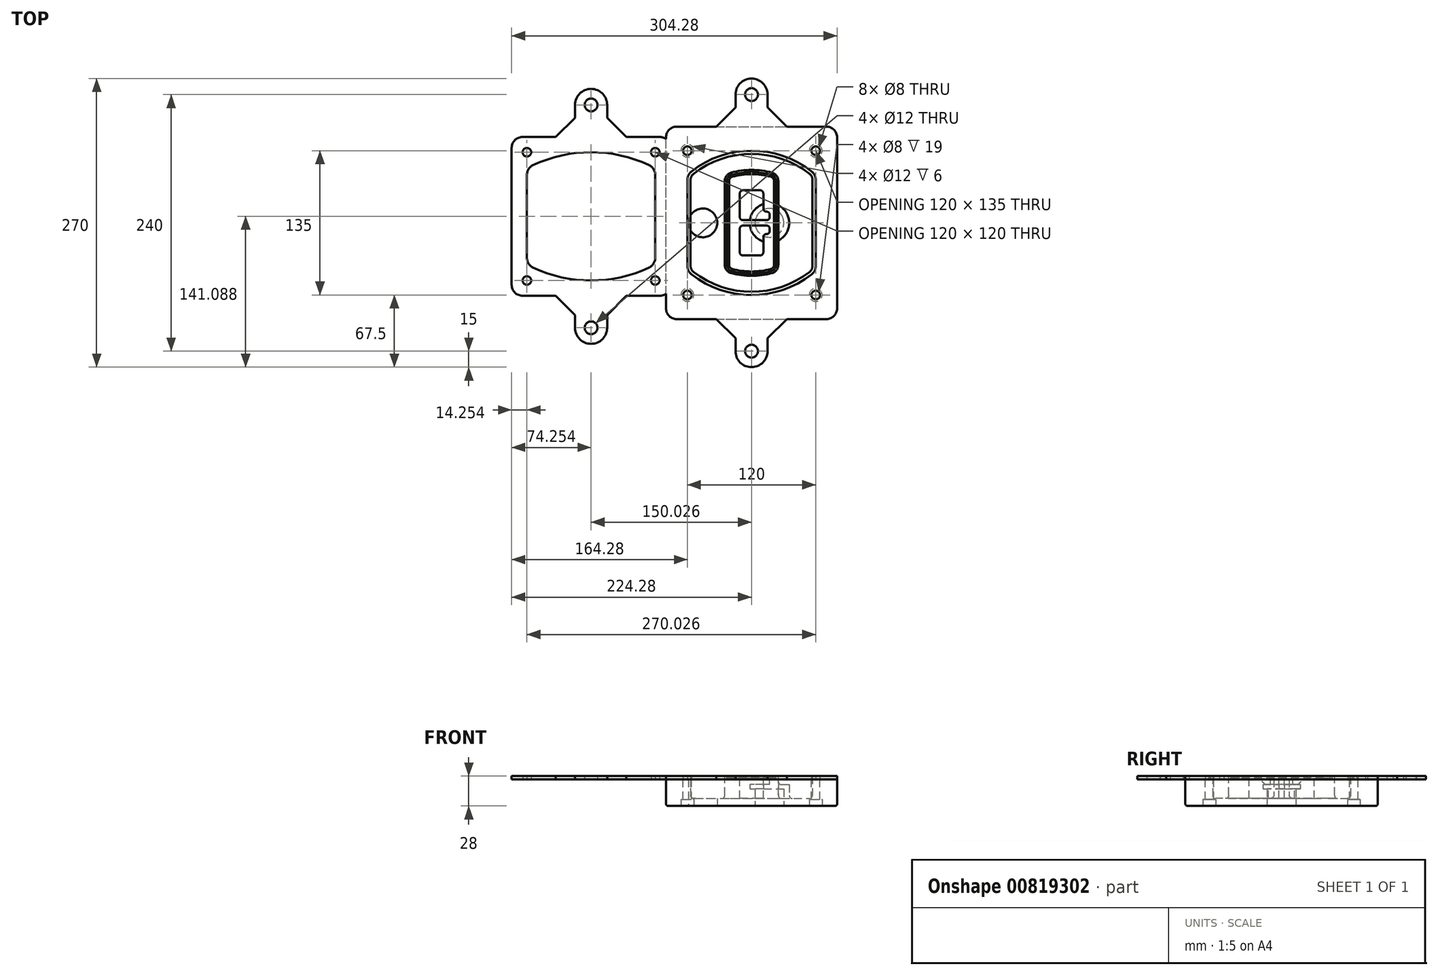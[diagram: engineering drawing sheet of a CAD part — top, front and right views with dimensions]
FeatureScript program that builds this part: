
annotation { "Feature Type Name" : "Feature", "Feature Type Description" : "" }
export const myFeature = defineFeature(function(context is Context, id is Id, definition is map)
    precondition{}
    {
        {
            var Q0;
            Q0=qCreatedBy(makeId("Top.planeOp"),FACE);
            var sketch = newSketch(context, id + "F0", { "sketchPlane" : qUnion([Q0])});
            skPoint(sketch, "E0.rect.middle", {"position": v(0, 0) * mm});
            skLineSegment(sketch, "E1.bottom", {"start": v(-70, -90) * mm, "end": v(70, -90) * mm});
            skLineSegment(sketch, "E1.top", {"start": v(-70, 90) * mm, "end": v(70, 90) * mm});
            skLineSegment(sketch, "E1.left", {"start": v(-80, -80) * mm, "end": v(-80, 80) * mm});
            skLineSegment(sketch, "E1.right", {"start": v(80, -80) * mm, "end": v(80, 80) * mm});
            skLineSegment(sketch, "E2", {"start": v(-80, 90) * mm, "end": v(80, -90) * mm, "construction": true});
            skLineSegment(sketch, "E3", {"start": v(80, 90) * mm, "end": v(-80, -90) * mm, "construction": true});
            skCircle(sketch, "E4", {"center": v(-60, 67.5) * mm, "radius": 4 * mm});
            skCircle(sketch, "E5", {"center": v(60, 67.5) * mm, "radius": 4 * mm});
            skCircle(sketch, "E6", {"center": v(60, -67.5) * mm, "radius": 4 * mm});
            skCircle(sketch, "E7", {"center": v(-60, -67.5) * mm, "radius": 4 * mm});
            skLineSegment(sketch, "E8", {"start": v(-60, 67.5) * mm, "end": v(60, 67.5) * mm, "construction": true});
            skLineSegment(sketch, "E9", {"start": v(60, 67.5) * mm, "end": v(60, -67.5) * mm, "construction": true});
            skLineSegment(sketch, "E10", {"start": v(60, -67.5) * mm, "end": v(-60, -67.5) * mm, "construction": true});
            skLineSegment(sketch, "E11", {"start": v(-60, -67.5) * mm, "end": v(-60, 67.5) * mm, "construction": true});
            skLineSegment(sketch, "E12", {"start": v(-60, 40.3) * mm, "end": v(-60, -40.3) * mm});
            skLineSegment(sketch, "E13", {"start": v(60, 40.3) * mm, "end": v(60, -40.3) * mm});
            skArc(sketch, "E14", {"start": v(56.15, 48.18) * mm, "mid": v(0, 67.5) * mm, "end": v(-56.15, 48.18) * mm});
            skArc(sketch, "E15", {"start": v(-56.15, -48.18) * mm, "mid": v(0, -67.5) * mm, "end": v(56.15, -48.18) * mm});
            skLineSegment(sketch, "E16", {"start": v(-60, 0) * mm, "end": v(60, 0) * mm, "construction": true});
            skPoint(sketch, "E17.visualSharp", {"position": v(-60, -45) * mm});
            skArc(sketch, "E17.filletArc", {"start": v(-60, -40.3) * mm, "mid": v(-58.99, -44.68) * mm, "end": v(-56.15, -48.18) * mm});
            skPoint(sketch, "E18.visualSharp", {"position": v(-60, 45) * mm});
            skArc(sketch, "E18.filletArc", {"start": v(-56.15, 48.18) * mm, "mid": v(-58.99, 44.68) * mm, "end": v(-60, 40.3) * mm});
            skPoint(sketch, "E19.visualSharp", {"position": v(60, 45) * mm});
            skArc(sketch, "E19.filletArc", {"start": v(60, 40.3) * mm, "mid": v(58.99, 44.68) * mm, "end": v(56.15, 48.18) * mm});
            skPoint(sketch, "E20.visualSharp", {"position": v(60, -45) * mm});
            skArc(sketch, "E20.filletArc", {"start": v(56.15, -48.18) * mm, "mid": v(58.99, -44.68) * mm, "end": v(60, -40.3) * mm});
            skPoint(sketch, "E21.visualSharp", {"position": v(-80, 90) * mm});
            skArc(sketch, "E21.filletArc", {"start": v(-70, 90) * mm, "mid": v(-77.07, 87.07) * mm, "end": v(-80, 80) * mm});
            skPoint(sketch, "E22.visualSharp", {"position": v(80, 90) * mm});
            skArc(sketch, "E22.filletArc", {"start": v(80, 80) * mm, "mid": v(77.07, 87.07) * mm, "end": v(70, 90) * mm});
            skPoint(sketch, "E23.visualSharp", {"position": v(80, -90) * mm});
            skArc(sketch, "E23.filletArc", {"start": v(70, -90) * mm, "mid": v(77.07, -87.07) * mm, "end": v(80, -80) * mm});
            skPoint(sketch, "E24.visualSharp", {"position": v(-80, -90) * mm});
            skArc(sketch, "E24.filletArc", {"start": v(-80, -80) * mm, "mid": v(-77.07, -87.07) * mm, "end": v(-70, -90) * mm});
            skArc(sketch, "E25.0", {"start": v(57, 40.3) * mm, "mid": v(56.3, 43.36) * mm, "end": v(54.3, 45.81) * mm});
            skLineSegment(sketch, "E25.1", {"start": v(57, 40.3) * mm, "end": v(57, -40.3) * mm});
            skArc(sketch, "E25.2", {"start": v(54.3, -45.81) * mm, "mid": v(56.3, -43.36) * mm, "end": v(57, -40.3) * mm});
            skArc(sketch, "E25.3", {"start": v(-54.3, -45.81) * mm, "mid": v(0, -64.5) * mm, "end": v(54.3, -45.81) * mm});
            skArc(sketch, "E25.4", {"start": v(-57, -40.3) * mm, "mid": v(-56.3, -43.36) * mm, "end": v(-54.3, -45.81) * mm});
            skArc(sketch, "E25.5", {"start": v(54.3, 45.81) * mm, "mid": v(0, 64.5) * mm, "end": v(-54.3, 45.81) * mm});
            skLineSegment(sketch, "E25.6", {"start": v(-57, 40.3) * mm, "end": v(-57, -40.3) * mm});
            skArc(sketch, "E25.7", {"start": v(-54.3, 45.81) * mm, "mid": v(-56.3, 43.36) * mm, "end": v(-57, 40.3) * mm});
            skArc(sketch, "E26.0", {"start": v(-58.62, 51.33) * mm, "mid": v(-62.58, 46.43) * mm, "end": v(-64, 40.3) * mm});
            skArc(sketch, "E26.1", {"start": v(58.62, 51.33) * mm, "mid": v(0, 71.5) * mm, "end": v(-58.62, 51.33) * mm});
            skArc(sketch, "E26.2", {"start": v(64, 40.3) * mm, "mid": v(62.58, 46.43) * mm, "end": v(58.62, 51.33) * mm});
            skLineSegment(sketch, "E26.3", {"start": v(64, 40.3) * mm, "end": v(64, -40.3) * mm});
            skArc(sketch, "E26.4", {"start": v(58.62, -51.33) * mm, "mid": v(62.58, -46.43) * mm, "end": v(64, -40.3) * mm});
            skLineSegment(sketch, "E26.5", {"start": v(-64, 40.3) * mm, "end": v(-64, -40.3) * mm});
            skArc(sketch, "E26.6", {"start": v(-58.62, -51.33) * mm, "mid": v(0, -71.5) * mm, "end": v(58.62, -51.33) * mm});
            skArc(sketch, "E26.7", {"start": v(-64, -40.3) * mm, "mid": v(-62.58, -46.43) * mm, "end": v(-58.62, -51.33) * mm});
            skSolve(sketch);
        }
        {
            var Q0;
            Q0=makeQuery(id+"F0.imprint","IMPRINT",FACE,{"disambiguationData":[TD([[makeQuery(id+"F0.imprint","IMPRINT",EDGE,{"derivedFrom":sQuery(id+"F0.wireOp",EDGE,"E1.bottom")}),1.0]])]});
            var Q1;
            Q1=makeQuery(id+"F0.imprint","IMPRINT",FACE,{"disambiguationData":[TD([[makeQuery(id+"F0.imprint","IMPRINT",EDGE,{"derivedFrom":sQuery(id+"F0.wireOp",EDGE,"E12")}),1.0]])]});
            var Q2;
            Q2=makeQuery(id+"F0.imprint","IMPRINT",FACE,{"disambiguationData":[TD([[makeQuery(id+"F0.imprint","IMPRINT",EDGE,{"derivedFrom":sQuery(id+"F0.wireOp",EDGE,"E25.0")}),1.0]])]});
            var Q3;
            Q3=makeQuery(id+"F0.imprint","IMPRINT",FACE,{"disambiguationData":[TD([[makeQuery(id+"F0.imprint","IMPRINT",EDGE,{"derivedFrom":sQuery(id+"F0.wireOp",EDGE,"E12")}),-1.0]])]});
            extrude(context, id + "F1", {"entities" : qUnion([Q0, Q1, Q2, Q3]), "oppositeDirection" : true, "depth" : 25 * mm});
        }
        {
            var Q0;
            Q0=makeQuery(id+"F0.imprint","IMPRINT",FACE,{"disambiguationData":[TD([[makeQuery(id+"F0.imprint","IMPRINT",EDGE,{"derivedFrom":sQuery(id+"F0.wireOp",EDGE,"E12")}),1.0]])]});
            extrude(context, id + "F2", {"entities" : qUnion([Q0]), "operationType" : NewBodyOperationType.ADD, "depth" : 3 * mm});
        }
        {
            var Q0;
            Q0=makeQuery(id+"F0.imprint","IMPRINT",FACE,{"disambiguationData":[TD([[makeQuery(id+"F0.imprint","IMPRINT",EDGE,{"derivedFrom":sQuery(id+"F0.wireOp",EDGE,"E25.0")}),1.0]])]});
            extrude(context, id + "F3", {"entities" : qUnion([Q0]), "operationType" : NewBodyOperationType.REMOVE, "oppositeDirection" : true, "depth" : 18 * mm});
        }
        {
            var Q0;
            Q0=makeQuery(id+"F2.opExtrude","CAP_FACE",FACE,{"disambiguationData":[OSD([sQuery(id+"F0.wireOp",EDGE,"E12"),sQuery(id+"F0.wireOp",EDGE,"E13"),sQuery(id+"F0.wireOp",EDGE,"E14"),sQuery(id+"F0.wireOp",EDGE,"E15"),sQuery(id+"F0.wireOp",EDGE,"E17.filletArc"),sQuery(id+"F0.wireOp",EDGE,"E18.filletArc"),sQuery(id+"F0.wireOp",EDGE,"E19.filletArc"),sQuery(id+"F0.wireOp",EDGE,"E20.filletArc"),sQuery(id+"F0.wireOp",EDGE,"E25.0"),sQuery(id+"F0.wireOp",EDGE,"E25.1"),sQuery(id+"F0.wireOp",EDGE,"E25.2"),sQuery(id+"F0.wireOp",EDGE,"E25.3"),sQuery(id+"F0.wireOp",EDGE,"E25.4"),sQuery(id+"F0.wireOp",EDGE,"E25.5"),sQuery(id+"F0.wireOp",EDGE,"E25.6"),sQuery(id+"F0.wireOp",EDGE,"E25.7")])],"isStart":false});
            var sketch = newSketch(context, id + "F4", { "sketchPlane" : qUnion([Q0])});
            skArc(sketch, "E27.0", {"start": v(-19.08, -46.97) * mm, "mid": v(0, -49.5) * mm, "end": v(19.08, -46.97) * mm});
            skArc(sketch, "E28.0", {"start": v(19.08, 46.97) * mm, "mid": v(0, 49.5) * mm, "end": v(-19.08, 46.97) * mm});
            skLineSegment(sketch, "E29", {"start": v(-25, 39.25) * mm, "end": v(-25, -39.25) * mm});
            skLineSegment(sketch, "E30", {"start": v(25, 39.25) * mm, "end": v(25, -39.25) * mm});
            skLineSegment(sketch, "E31", {"start": v(-25, 45.1) * mm, "end": v(25, 45.1) * mm, "construction": true});
            skLineSegment(sketch, "E32", {"start": v(-25, -45.1) * mm, "end": v(25, -45.1) * mm, "construction": true});
            skPoint(sketch, "E33.visualSharp", {"position": v(-25, 45.1) * mm});
            skArc(sketch, "E33.filletArc", {"start": v(-19.08, 46.97) * mm, "mid": v(-23.35, 44.11) * mm, "end": v(-25, 39.25) * mm});
            skPoint(sketch, "E34.visualSharp", {"position": v(25, 45.1) * mm});
            skArc(sketch, "E34.filletArc", {"start": v(25, 39.25) * mm, "mid": v(23.35, 44.11) * mm, "end": v(19.08, 46.97) * mm});
            skPoint(sketch, "E35.visualSharp", {"position": v(25, -45.1) * mm});
            skArc(sketch, "E35.filletArc", {"start": v(19.08, -46.97) * mm, "mid": v(23.35, -44.11) * mm, "end": v(25, -39.25) * mm});
            skPoint(sketch, "E36.visualSharp", {"position": v(-25, -45.1) * mm});
            skArc(sketch, "E36.filletArc", {"start": v(-25, -39.25) * mm, "mid": v(-23.35, -44.11) * mm, "end": v(-19.08, -46.97) * mm});
            skArc(sketch, "E37.0", {"start": v(54.3, 45.81) * mm, "mid": v(0, 64.5) * mm, "end": v(-54.3, 45.81) * mm});
            skArc(sketch, "E37.1", {"start": v(-54.3, 45.81) * mm, "mid": v(-56.3, 43.36) * mm, "end": v(-57, 40.3) * mm});
            skLineSegment(sketch, "E37.2", {"start": v(-57, 40.3) * mm, "end": v(-57, -40.3) * mm});
            skArc(sketch, "E37.3", {"start": v(-57, -40.3) * mm, "mid": v(-56.3, -43.36) * mm, "end": v(-54.3, -45.81) * mm});
            skArc(sketch, "E37.4", {"start": v(-54.3, -45.81) * mm, "mid": v(0, -64.5) * mm, "end": v(54.3, -45.81) * mm});
            skArc(sketch, "E37.5", {"start": v(54.3, -45.81) * mm, "mid": v(56.3, -43.36) * mm, "end": v(57, -40.3) * mm});
            skLineSegment(sketch, "E37.6", {"start": v(57, 40.3) * mm, "end": v(57, -40.3) * mm});
            skArc(sketch, "E37.7", {"start": v(57, 40.3) * mm, "mid": v(56.3, 43.36) * mm, "end": v(54.3, 45.81) * mm});
            skLineSegment(sketch, "E38.0", {"start": v(23, 39.25) * mm, "end": v(23, -39.25) * mm});
            skArc(sketch, "E38.1", {"start": v(18.56, -45.04) * mm, "mid": v(21.76, -42.9) * mm, "end": v(23, -39.25) * mm});
            skArc(sketch, "E38.2", {"start": v(-18.56, -45.04) * mm, "mid": v(0, -47.5) * mm, "end": v(18.56, -45.04) * mm});
            skArc(sketch, "E38.3", {"start": v(-23, -39.25) * mm, "mid": v(-21.76, -42.9) * mm, "end": v(-18.56, -45.04) * mm});
            skLineSegment(sketch, "E38.4", {"start": v(-23, 39.25) * mm, "end": v(-23, -39.25) * mm});
            skArc(sketch, "E38.5", {"start": v(23, 39.25) * mm, "mid": v(21.76, 42.9) * mm, "end": v(18.56, 45.04) * mm});
            skArc(sketch, "E38.6", {"start": v(-18.56, 45.04) * mm, "mid": v(-21.76, 42.9) * mm, "end": v(-23, 39.25) * mm});
            skArc(sketch, "E38.7", {"start": v(18.56, 45.04) * mm, "mid": v(0, 47.5) * mm, "end": v(-18.56, 45.04) * mm});
            skArc(sketch, "E39.0", {"start": v(21, 39.25) * mm, "mid": v(20.18, 41.68) * mm, "end": v(18.04, 43.1) * mm});
            skLineSegment(sketch, "E39.1", {"start": v(21, 39.25) * mm, "end": v(21, -39.25) * mm});
            skArc(sketch, "E39.2", {"start": v(18.04, -43.1) * mm, "mid": v(20.18, -41.68) * mm, "end": v(21, -39.25) * mm});
            skArc(sketch, "E39.3", {"start": v(-18.04, -43.1) * mm, "mid": v(0, -45.5) * mm, "end": v(18.04, -43.1) * mm});
            skArc(sketch, "E39.4", {"start": v(-21, -39.25) * mm, "mid": v(-20.18, -41.68) * mm, "end": v(-18.04, -43.1) * mm});
            skArc(sketch, "E39.5", {"start": v(18.04, 43.1) * mm, "mid": v(0, 45.5) * mm, "end": v(-18.04, 43.1) * mm});
            skLineSegment(sketch, "E39.6", {"start": v(-21, 39.25) * mm, "end": v(-21, -39.25) * mm});
            skArc(sketch, "E39.7", {"start": v(-18.04, 43.1) * mm, "mid": v(-20.18, 41.68) * mm, "end": v(-21, 39.25) * mm});
            skLineSegment(sketch, "E40", {"start": v(-25, 0) * mm, "end": v(25, 0) * mm, "construction": true});
            skLineSegment(sketch, "E41", {"start": v(-11, 5.5) * mm, "end": v(-11, 27.5) * mm});
            skLineSegment(sketch, "E42", {"start": v(-8, 30.5) * mm, "end": v(8, 30.5) * mm});
            skLineSegment(sketch, "E43", {"start": v(11, 27.5) * mm, "end": v(11, 13.5) * mm});
            skLineSegment(sketch, "E44", {"start": v(14, 10.5) * mm, "end": v(14, 10.5) * mm});
            skLineSegment(sketch, "E45", {"start": v(17, 7.5) * mm, "end": v(17, 5.5) * mm});
            skLineSegment(sketch, "E46", {"start": v(14, 2.5) * mm, "end": v(-8, 2.5) * mm});
            skPoint(sketch, "E47.visualSharp", {"position": v(-11, 30.5) * mm});
            skArc(sketch, "E47.filletArc", {"start": v(-8, 30.5) * mm, "mid": v(-10.12, 29.62) * mm, "end": v(-11, 27.5) * mm});
            skPoint(sketch, "E48.visualSharp", {"position": v(11, 30.5) * mm});
            skArc(sketch, "E48.filletArc", {"start": v(11, 27.5) * mm, "mid": v(10.12, 29.62) * mm, "end": v(8, 30.5) * mm});
            skPoint(sketch, "E49.visualSharp", {"position": v(11, 10.5) * mm});
            skArc(sketch, "E49.filletArc", {"start": v(11, 13.5) * mm, "mid": v(11.88, 11.38) * mm, "end": v(14, 10.5) * mm});
            skPoint(sketch, "E50.visualSharp", {"position": v(17, 10.5) * mm});
            skArc(sketch, "E50.filletArc", {"start": v(17, 7.5) * mm, "mid": v(16.12, 9.62) * mm, "end": v(14, 10.5) * mm});
            skPoint(sketch, "E51.visualSharp", {"position": v(17, 2.5) * mm});
            skArc(sketch, "E51.filletArc", {"start": v(14, 2.5) * mm, "mid": v(16.12, 3.38) * mm, "end": v(17, 5.5) * mm});
            skPoint(sketch, "E52.visualSharp", {"position": v(-11, 2.5) * mm});
            skArc(sketch, "E52.filletArc", {"start": v(-11, 5.5) * mm, "mid": v(-10.12, 3.38) * mm, "end": v(-8, 2.5) * mm});
            skLineSegment(sketch, "E53.0.MirrorCS", {"start": v(14, -2.5) * mm, "end": v(-8, -2.5) * mm});
            skArc(sketch, "E54.0.MirrorCS", {"start": v(-11, -5.5) * mm, "mid": v(-10.12, -3.38) * mm, "end": v(-8, -2.5) * mm});
            skLineSegment(sketch, "E55.0.MirrorCS", {"start": v(-11, -5.5) * mm, "end": v(-11, -27.5) * mm});
            skArc(sketch, "E56.0.MirrorCS", {"start": v(-8, -30.5) * mm, "mid": v(-10.12, -29.62) * mm, "end": v(-11, -27.5) * mm});
            skLineSegment(sketch, "E57.0.MirrorCS", {"start": v(-8, -30.5) * mm, "end": v(8, -30.5) * mm});
            skArc(sketch, "E58.0.MirrorCS", {"start": v(11, -27.5) * mm, "mid": v(10.12, -29.62) * mm, "end": v(8, -30.5) * mm});
            skLineSegment(sketch, "E59.0.MirrorCS", {"start": v(11, -27.5) * mm, "end": v(11, -13.5) * mm});
            skArc(sketch, "E60.0.MirrorCS", {"start": v(11, -13.5) * mm, "mid": v(11.88, -11.38) * mm, "end": v(14, -10.5) * mm});
            skArc(sketch, "E61.0.MirrorCS", {"start": v(17, -7.5) * mm, "mid": v(16.12, -9.62) * mm, "end": v(14, -10.5) * mm});
            skLineSegment(sketch, "E62.0.MirrorCS", {"start": v(17, -7.5) * mm, "end": v(17, -5.5) * mm});
            skArc(sketch, "E63.0.MirrorCS", {"start": v(14, -2.5) * mm, "mid": v(16.12, -3.38) * mm, "end": v(17, -5.5) * mm});
            skSolve(sketch);
        }
        {
            var Q0;
            Q0=makeQuery(id+"F4.imprint","IMPRINT",FACE,{"disambiguationData":[TD([[makeQuery(id+"F4.imprint","IMPRINT",EDGE,{"derivedFrom":sQuery(id+"F4.wireOp",EDGE,"E27.0")}),1.0]])]});
            var Q1;
            Q1=makeQuery(id+"F4.imprint","IMPRINT",FACE,{"disambiguationData":[TD([[makeQuery(id+"F4.imprint","IMPRINT",EDGE,{"derivedFrom":sQuery(id+"F4.wireOp",EDGE,"E38.0")}),-1.0]])]});
            var Q2;
            Q2=makeQuery(id+"F4.imprint","IMPRINT",FACE,{"disambiguationData":[TD([[makeQuery(id+"F4.imprint","IMPRINT",EDGE,{"derivedFrom":sQuery(id+"F4.wireOp",EDGE,"E39.0")}),1.0]])]});
            extrude(context, id + "F5", {"entities" : qUnion([Q0, Q1, Q2]), "operationType" : NewBodyOperationType.ADD, "endBound" : BoundingType.UP_TO_NEXT, "oppositeDirection" : true, "depth" : 25 * mm});
        }
        {
            var Q0;
            Q0=makeQuery(id+"F4.imprint","IMPRINT",FACE,{"disambiguationData":[TD([[makeQuery(id+"F4.imprint","IMPRINT",EDGE,{"derivedFrom":sQuery(id+"F4.wireOp",EDGE,"E38.0")}),-1.0]])]});
            extrude(context, id + "F6", {"entities" : qUnion([Q0]), "operationType" : NewBodyOperationType.REMOVE, "oppositeDirection" : true, "depth" : 2 * mm});
        }
        {
            var Q0;
            Q0=makeQuery(id+"F1.opExtrude","CAP_FACE",FACE,{"disambiguationData":[OSD([sQuery(id+"F0.wireOp",EDGE,"E1.bottom"),sQuery(id+"F0.wireOp",EDGE,"E1.top"),sQuery(id+"F0.wireOp",EDGE,"E1.left"),sQuery(id+"F0.wireOp",EDGE,"E1.right"),sQuery(id+"F0.wireOp",EDGE,"E4"),sQuery(id+"F0.wireOp",EDGE,"E5"),sQuery(id+"F0.wireOp",EDGE,"E6"),sQuery(id+"F0.wireOp",EDGE,"E7"),sQuery(id+"F0.wireOp",EDGE,"E21.filletArc"),sQuery(id+"F0.wireOp",EDGE,"E22.filletArc"),sQuery(id+"F0.wireOp",EDGE,"E23.filletArc"),sQuery(id+"F0.wireOp",EDGE,"E24.filletArc")])],"isStart":false});
            var sketch = newSketch(context, id + "F7", { "sketchPlane" : qUnion([Q0])});
            skCircle(sketch, "E64", {"center": v(16.76, 0) * mm, "radius": 13.47 * mm});
            skCircle(sketch, "E65", {"center": v(-45.56, 0) * mm, "radius": 13.47 * mm});
            skLineSegment(sketch, "E66", {"start": v(80, 0) * mm, "end": v(-80, 0) * mm});
            skCircle(sketch, "E67", {"center": v(16.76, 0) * mm, "radius": 18.47 * mm});
            skCircle(sketch, "E68", {"center": v(60, -67.5) * mm, "radius": 6 * mm});
            skCircle(sketch, "E69", {"center": v(-60, -67.5) * mm, "radius": 6 * mm});
            skCircle(sketch, "E70", {"center": v(-60, 67.5) * mm, "radius": 6 * mm});
            skCircle(sketch, "E71", {"center": v(60, 67.5) * mm, "radius": 6 * mm});
            skSolve(sketch);
        }
        {
            var Q0;
            {var subQ1=sQuery(id+"F7.wireOp",EDGE,"E66");var subQ4=sQuery(id+"F7.wireOp",EDGE,"E64");var subQ6=makeQuery(id+"F7.imprint","INTERSECT",VERTEX,{"disambiguationData":[OD(0.0)],"derivedFrom":[subQ4,subQ1]});Q0=makeQuery(id+"F7.imprint","IMPRINT",FACE,{"disambiguationData":[TD([[makeQuery(id+"F7.imprint","IMPRINT",EDGE,{"disambiguationData":[TD([[subQ6,-1.0]])],"derivedFrom":subQ4}),-1.0]])]});}
            var Q1;
            {var subQ0=sQuery(id+"F7.wireOp",EDGE,"E66");var subQ1=sQuery(id+"F7.wireOp",EDGE,"E64");var subQ3=makeQuery(id+"F7.imprint","INTERSECT",VERTEX,{"disambiguationData":[OD(0.0)],"derivedFrom":[subQ1,subQ0]});Q1=makeQuery(id+"F7.imprint","IMPRINT",FACE,{"disambiguationData":[TD([[makeQuery(id+"F7.imprint","IMPRINT",EDGE,{"disambiguationData":[TD([[subQ3,-1.0]])],"derivedFrom":subQ1}),1.0]])]});}
            var Q2;
            {var subQ0=sQuery(id+"F7.wireOp",EDGE,"E66");var subQ1=sQuery(id+"F7.wireOp",EDGE,"E64");var subQ3=makeQuery(id+"F7.imprint","INTERSECT",VERTEX,{"disambiguationData":[OD(0.0)],"derivedFrom":[subQ1,subQ0]});Q2=makeQuery(id+"F7.imprint","IMPRINT",FACE,{"disambiguationData":[TD([[makeQuery(id+"F7.imprint","IMPRINT",EDGE,{"disambiguationData":[TD([[subQ3,1.0]])],"derivedFrom":subQ1}),1.0]])]});}
            var Q3;
            {var subQ1=sQuery(id+"F7.wireOp",EDGE,"E66");var subQ4=sQuery(id+"F7.wireOp",EDGE,"E64");var subQ6=makeQuery(id+"F7.imprint","INTERSECT",VERTEX,{"disambiguationData":[OD(0.0)],"derivedFrom":[subQ4,subQ1]});Q3=makeQuery(id+"F7.imprint","IMPRINT",FACE,{"disambiguationData":[TD([[makeQuery(id+"F7.imprint","IMPRINT",EDGE,{"disambiguationData":[TD([[subQ6,1.0]])],"derivedFrom":subQ4}),-1.0]])]});}
            extrude(context, id + "F8", {"entities" : qUnion([Q0, Q1, Q2, Q3]), "operationType" : NewBodyOperationType.ADD, "oppositeDirection" : true, "depth" : 20 * mm});
        }
        {
            var Q0;
            {var subQ0=sQuery(id+"F7.wireOp",EDGE,"E66");var subQ1=sQuery(id+"F7.wireOp",EDGE,"E64");var subQ3=makeQuery(id+"F7.imprint","INTERSECT",VERTEX,{"disambiguationData":[OD(0.0)],"derivedFrom":[subQ1,subQ0]});Q0=makeQuery(id+"F7.imprint","IMPRINT",FACE,{"disambiguationData":[TD([[makeQuery(id+"F7.imprint","IMPRINT",EDGE,{"disambiguationData":[TD([[subQ3,-1.0]])],"derivedFrom":subQ1}),1.0]])]});}
            var Q1;
            {var subQ0=sQuery(id+"F7.wireOp",EDGE,"E66");var subQ1=sQuery(id+"F7.wireOp",EDGE,"E64");var subQ3=makeQuery(id+"F7.imprint","INTERSECT",VERTEX,{"disambiguationData":[OD(0.0)],"derivedFrom":[subQ1,subQ0]});Q1=makeQuery(id+"F7.imprint","IMPRINT",FACE,{"disambiguationData":[TD([[makeQuery(id+"F7.imprint","IMPRINT",EDGE,{"disambiguationData":[TD([[subQ3,1.0]])],"derivedFrom":subQ1}),1.0]])]});}
            extrude(context, id + "F9", {"entities" : qUnion([Q0, Q1]), "operationType" : NewBodyOperationType.REMOVE, "oppositeDirection" : true, "depth" : 16 * mm});
        }
        {
            var Q0;
            {var subQ0=sQuery(id+"F7.wireOp",EDGE,"E66");var subQ1=sQuery(id+"F7.wireOp",EDGE,"E65");var subQ3=makeQuery(id+"F7.imprint","INTERSECT",VERTEX,{"disambiguationData":[OD(0.0)],"derivedFrom":[subQ1,subQ0]});Q0=makeQuery(id+"F7.imprint","IMPRINT",FACE,{"disambiguationData":[TD([[makeQuery(id+"F7.imprint","IMPRINT",EDGE,{"disambiguationData":[TD([[subQ3,-1.0]])],"derivedFrom":subQ1}),1.0]])]});}
            var Q1;
            {var subQ0=sQuery(id+"F7.wireOp",EDGE,"E66");var subQ1=sQuery(id+"F7.wireOp",EDGE,"E65");var subQ3=makeQuery(id+"F7.imprint","INTERSECT",VERTEX,{"disambiguationData":[OD(0.0)],"derivedFrom":[subQ1,subQ0]});Q1=makeQuery(id+"F7.imprint","IMPRINT",FACE,{"disambiguationData":[TD([[makeQuery(id+"F7.imprint","IMPRINT",EDGE,{"disambiguationData":[TD([[subQ3,1.0]])],"derivedFrom":subQ1}),1.0]])]});}
            extrude(context, id + "F10", {"entities" : qUnion([Q0, Q1]), "operationType" : NewBodyOperationType.REMOVE, "oppositeDirection" : true, "depth" : 25 * mm});
        }
        {
            var Q0;
            Q0=makeQuery(id+"F7.imprint","IMPRINT",FACE,{"disambiguationData":[TD([[makeQuery(id+"F7.imprint","IMPRINT",EDGE,{"derivedFrom":sQuery(id+"F7.wireOp",EDGE,"E68")}),1.0]])]});
            var Q1;
            Q1=makeQuery(id+"F7.imprint","IMPRINT",FACE,{"disambiguationData":[TD([[makeQuery(id+"F7.imprint","IMPRINT",EDGE,{"derivedFrom":makeQuery(id+"F1.opExtrude","CAP_EDGE",EDGE,{"disambiguationData":[OSD([sQuery(id+"F0.wireOp",EDGE,"E5")])],"isStart":false})}),-1.0]])]});
            var Q2;
            Q2=makeQuery(id+"F7.imprint","IMPRINT",FACE,{"disambiguationData":[TD([[makeQuery(id+"F7.imprint","IMPRINT",EDGE,{"derivedFrom":sQuery(id+"F7.wireOp",EDGE,"E69")}),1.0]])]});
            var Q3;
            Q3=makeQuery(id+"F7.imprint","IMPRINT",FACE,{"disambiguationData":[TD([[makeQuery(id+"F7.imprint","IMPRINT",EDGE,{"derivedFrom":makeQuery(id+"F1.opExtrude","CAP_EDGE",EDGE,{"disambiguationData":[OSD([sQuery(id+"F0.wireOp",EDGE,"E4")])],"isStart":false})}),-1.0]])]});
            var Q4;
            Q4=makeQuery(id+"F7.imprint","IMPRINT",FACE,{"disambiguationData":[TD([[makeQuery(id+"F7.imprint","IMPRINT",EDGE,{"derivedFrom":sQuery(id+"F7.wireOp",EDGE,"E70")}),1.0]])]});
            var Q5;
            Q5=makeQuery(id+"F7.imprint","IMPRINT",FACE,{"disambiguationData":[TD([[makeQuery(id+"F7.imprint","IMPRINT",EDGE,{"derivedFrom":makeQuery(id+"F1.opExtrude","CAP_EDGE",EDGE,{"disambiguationData":[OSD([sQuery(id+"F0.wireOp",EDGE,"E7")])],"isStart":false})}),-1.0]])]});
            var Q6;
            Q6=makeQuery(id+"F7.imprint","IMPRINT",FACE,{"disambiguationData":[TD([[makeQuery(id+"F7.imprint","IMPRINT",EDGE,{"derivedFrom":sQuery(id+"F7.wireOp",EDGE,"E71")}),1.0]])]});
            var Q7;
            Q7=makeQuery(id+"F7.imprint","IMPRINT",FACE,{"disambiguationData":[TD([[makeQuery(id+"F7.imprint","IMPRINT",EDGE,{"derivedFrom":makeQuery(id+"F1.opExtrude","CAP_EDGE",EDGE,{"disambiguationData":[OSD([sQuery(id+"F0.wireOp",EDGE,"E6")])],"isStart":false})}),-1.0]])]});
            extrude(context, id + "F11", {"entities" : qUnion([Q0, Q1, Q2, Q3, Q4, Q5, Q6, Q7]), "operationType" : NewBodyOperationType.REMOVE, "oppositeDirection" : true, "depth" : 6 * mm});
        }
        {
            var Q0;
            Q0=makeQuery(id+"F9.boolean.opBoolean","COPY",FACE,{"derivedFrom":makeQuery(id+"F9.opExtrude","CAP_FACE",FACE,{"disambiguationData":[OSD([sQuery(id+"F7.wireOp",EDGE,"E64")])],"isStart":false})});
            var sketch = newSketch(context, id + "F12", { "sketchPlane" : qUnion([Q0])});
            skArc(sketch, "E72.0", {"start": v(11, 17.55) * mm, "mid": v(2.57, 11.82) * mm, "end": v(-1.54, 2.5) * mm});
            skArc(sketch, "E72.1", {"start": v(-1.54, -2.5) * mm, "mid": v(2.57, -11.82) * mm, "end": v(11, -17.55) * mm});
            skLineSegment(sketch, "E73", {"start": v(-1.54, -2.5) * mm, "end": v(14, -2.5) * mm});
            skLineSegment(sketch, "E74.0", {"start": v(14, 2.5) * mm, "end": v(-1.54, 2.5) * mm});
            skArc(sketch, "E74.1", {"start": v(14, 2.5) * mm, "mid": v(16.12, 3.38) * mm, "end": v(17, 5.5) * mm});
            skLineSegment(sketch, "E74.2", {"start": v(17, 7.5) * mm, "end": v(17, 5.5) * mm});
            skArc(sketch, "E74.3", {"start": v(17, 7.5) * mm, "mid": v(16.12, 9.62) * mm, "end": v(14, 10.5) * mm});
            skArc(sketch, "E74.4", {"start": v(11, 13.5) * mm, "mid": v(11.88, 11.38) * mm, "end": v(14, 10.5) * mm});
            skLineSegment(sketch, "E74.5", {"start": v(11, 17.55) * mm, "end": v(11, 13.5) * mm});
            skLineSegment(sketch, "E74.7", {"start": v(14, -2.5) * mm, "end": v(-1.54, -2.5) * mm});
            skArc(sketch, "E74.8", {"start": v(14, -2.5) * mm, "mid": v(16.12, -3.38) * mm, "end": v(17, -5.5) * mm});
            skLineSegment(sketch, "E74.9", {"start": v(17, -7.5) * mm, "end": v(17, -5.5) * mm});
            skArc(sketch, "E74.10", {"start": v(17, -7.5) * mm, "mid": v(16.12, -9.62) * mm, "end": v(14, -10.5) * mm});
            skArc(sketch, "E74.11", {"start": v(11, -13.5) * mm, "mid": v(11.88, -11.38) * mm, "end": v(14, -10.5) * mm});
            skLineSegment(sketch, "E74.12", {"start": v(11, -17.55) * mm, "end": v(11, -13.5) * mm});
            skPoint(sketch, "E75.orphan", {"position": v(11, -27.5) * mm});
            skPoint(sketch, "E76.orphan", {"position": v(-8, -2.5) * mm});
            skPoint(sketch, "E77.orphan", {"position": v(-8, 2.5) * mm});
            skPoint(sketch, "E78.orphan", {"position": v(11, 27.5) * mm});
            skSolve(sketch);
        }
        {
            var Q0;
            {var subQ7=sQuery(id+"F12.wireOp",EDGE,"E72.0");var subQ14=sQuery(id+"F12.wireOp",EDGE,"E72.1");var subQ16=sQuery(id+"F12.wireOp",EDGE,"E74.1");var subQ18=sQuery(id+"F12.wireOp",EDGE,"E74.8");Q0=qUnion([makeQuery(id+"F12.imprint","IMPRINT",FACE,{"disambiguationData":[TD([[makeQuery(id+"F12.imprint","IMPRINT",EDGE,{"derivedFrom":subQ7}),1.0]])]}),makeQuery(id+"F12.imprint","IMPRINT",FACE,{"disambiguationData":[TD([[makeQuery(id+"F12.imprint","IMPRINT",EDGE,{"derivedFrom":subQ14}),1.0]])]}),makeQuery(id+"F12.imprint","IMPRINT",FACE,{"disambiguationData":[TD([[makeQuery(id+"F12.imprint","IMPRINT",EDGE,{"derivedFrom":subQ16}),1.0]])]}),makeQuery(id+"F12.imprint","IMPRINT",FACE,{"disambiguationData":[TD([[makeQuery(id+"F12.imprint","IMPRINT",EDGE,{"derivedFrom":subQ18}),-1.0]])]})]);}
            var Q1;
            Q1=makeQuery(id+"F5.boolean.opBoolean","SPLIT",FACE,{"disambiguationData":[TD([makeQuery(id+"F5.opExtrude","SWEPT_FACE",FACE,{"disambiguationData":[OSD([sQuery(id+"F4.wireOp",EDGE,"E41")])]})])],"derivedFrom":makeQuery(id+"F3.boolean.opBoolean","COPY",FACE,{"derivedFrom":makeQuery(id+"F3.opExtrude","CAP_FACE",FACE,{"disambiguationData":[OSD([sQuery(id+"F0.wireOp",EDGE,"E25.0"),sQuery(id+"F0.wireOp",EDGE,"E25.1"),sQuery(id+"F0.wireOp",EDGE,"E25.2"),sQuery(id+"F0.wireOp",EDGE,"E25.3"),sQuery(id+"F0.wireOp",EDGE,"E25.4"),sQuery(id+"F0.wireOp",EDGE,"E25.5"),sQuery(id+"F0.wireOp",EDGE,"E25.6"),sQuery(id+"F0.wireOp",EDGE,"E25.7")])],"isStart":false})})});
            extrude(context, id + "F13", {"entities" : qUnion([Q0]), "operationType" : NewBodyOperationType.REMOVE, "endBound" : BoundingType.UP_TO_SURFACE, "endBoundEntityFace" : qUnion([Q1]), "depth" : 25 * mm});
        }
        {
            var Q0;
            Q0=makeQuery(id+"F3.boolean.opBoolean","COPY",EDGE,{"derivedFrom":makeQuery(id+"F3.opExtrude","CAP_EDGE",EDGE,{"disambiguationData":[OSD([sQuery(id+"F0.wireOp",EDGE,"E25.6")])],"isStart":false})});
            var Q1;
            Q1=makeQuery(id+"F8.boolean.opBoolean","INTERSECT",EDGE,{"derivedFrom":[makeQuery(id+"F5.opExtrude","SWEPT_FACE",FACE,{"disambiguationData":[OSD([sQuery(id+"F4.wireOp",EDGE,"E30")])]}),makeQuery(id+"F8.opExtrude","CAP_FACE",FACE,{"disambiguationData":[OSD([sQuery(id+"F7.wireOp",EDGE,"E67")])],"isStart":false})]});
            var Q2;
            Q2=makeQuery(id+"F8.boolean.opBoolean","INTERSECT",EDGE,{"disambiguationData":[OD(1.0)],"derivedFrom":[makeQuery(id+"F5.opExtrude","SWEPT_FACE",FACE,{"disambiguationData":[OSD([sQuery(id+"F4.wireOp",EDGE,"E30")])]}),makeQuery(id+"F8.opExtrude","SWEPT_FACE",FACE,{"disambiguationData":[OSD([sQuery(id+"F7.wireOp",EDGE,"E67")])]})]});
            var Q3;
            {var subQ0=sQuery(id+"F4.wireOp",EDGE,"E30");Q3=makeQuery(id+"F8.boolean.opBoolean","SPLIT",EDGE,{"disambiguationData":[TD([makeQuery(id+"F5.opExtrude","SWEPT_FACE",FACE,{"disambiguationData":[OSD([sQuery(id+"F4.wireOp",EDGE,"E35.filletArc")])]})])],"derivedFrom":makeQuery(id+"F5.opExtrude","CAP_EDGE",EDGE,{"disambiguationData":[OSD([subQ0])],"isStart":false})});}
            var Q4;
            {var subQ0=sQuery(id+"F0.wireOp",EDGE,"E25.7");var subQ1=sQuery(id+"F0.wireOp",EDGE,"E25.1");var subQ2=sQuery(id+"F0.wireOp",EDGE,"E25.6");var subQ3=sQuery(id+"F0.wireOp",EDGE,"E25.5");var subQ4=sQuery(id+"F0.wireOp",EDGE,"E25.4");var subQ5=sQuery(id+"F0.wireOp",EDGE,"E25.0");var subQ6=sQuery(id+"F0.wireOp",EDGE,"E25.2");var subQ7=sQuery(id+"F0.wireOp",EDGE,"E25.3");Q4=makeQuery(id+"F8.boolean.opBoolean","INTERSECT",EDGE,{"derivedFrom":[makeQuery(id+"F5.boolean.opBoolean","SPLIT",FACE,{"disambiguationData":[TD([makeQuery(id+"F2.opExtrude","SWEPT_FACE",FACE,{"disambiguationData":[OSD([subQ5])]})])],"derivedFrom":makeQuery(id+"F3.boolean.opBoolean","COPY",FACE,{"derivedFrom":makeQuery(id+"F3.opExtrude","CAP_FACE",FACE,{"disambiguationData":[OSD([subQ5,subQ1,subQ6,subQ7,subQ4,subQ3,subQ2,subQ0])],"isStart":false})})}),makeQuery(id+"F8.opExtrude","SWEPT_FACE",FACE,{"disambiguationData":[OSD([sQuery(id+"F7.wireOp",EDGE,"E67")])]})]});}
            var Q5;
            Q5=makeQuery(id+"F8.boolean.opBoolean","INTERSECT",EDGE,{"disambiguationData":[OD(0.0)],"derivedFrom":[makeQuery(id+"F5.opExtrude","SWEPT_FACE",FACE,{"disambiguationData":[OSD([sQuery(id+"F4.wireOp",EDGE,"E30")])]}),makeQuery(id+"F8.opExtrude","SWEPT_FACE",FACE,{"disambiguationData":[OSD([sQuery(id+"F7.wireOp",EDGE,"E67")])]})]});
            fillet(context, id + "F14", {"entities" : qUnion([Q0, Q1, Q2, Q3, Q4, Q5]), "radius" : 3 * mm, "tangentPropagation" : true, "allowEdgeOverflow" : false});
        }
        {
            var Q0;
            Q0=makeQuery(id+"F1.opExtrude","CAP_EDGE",EDGE,{"disambiguationData":[OSD([sQuery(id+"F0.wireOp",EDGE,"E1.bottom")])],"isStart":false});
            fillet(context, id + "F15", {"entities" : qUnion([Q0]), "radius" : 2 * mm, "tangentPropagation" : true, "allowEdgeOverflow" : false});
        }
        {
            var Q0;
            {var subQ0=sQuery(id+"F0.wireOp",EDGE,"E21.filletArc");var subQ1=sQuery(id+"F0.wireOp",EDGE,"E7");var subQ2=sQuery(id+"F0.wireOp",EDGE,"E6");var subQ3=sQuery(id+"F0.wireOp",EDGE,"E5");var subQ4=sQuery(id+"F0.wireOp",EDGE,"E4");var subQ5=sQuery(id+"F0.wireOp",EDGE,"E22.filletArc");var subQ6=sQuery(id+"F0.wireOp",EDGE,"E1.bottom");var subQ7=sQuery(id+"F0.wireOp",EDGE,"E1.right");var subQ8=sQuery(id+"F0.wireOp",EDGE,"E1.top");var subQ9=sQuery(id+"F0.wireOp",EDGE,"E1.left");var subQ10=sQuery(id+"F0.wireOp",EDGE,"E23.filletArc");var subQ11=sQuery(id+"F0.wireOp",EDGE,"E24.filletArc");Q0=makeQuery(id+"F2.boolean.opBoolean","SPLIT",FACE,{"disambiguationData":[TD([makeQuery(id+"F1.opExtrude","SWEPT_FACE",FACE,{"disambiguationData":[OSD([subQ6])]})])],"derivedFrom":makeQuery(id+"F1.opExtrude","CAP_FACE",FACE,{"disambiguationData":[OSD([subQ6,subQ8,subQ9,subQ7,subQ4,subQ3,subQ2,subQ1,subQ0,subQ5,subQ10,subQ11])],"isStart":true})});}
            var sketch = newSketch(context, id + "F16", { "sketchPlane" : qUnion([Q0])});
            skCircle(sketch, "E79.0", {"center": v(60, 67.5) * mm, "radius": 4 * mm});
            skLineSegment(sketch, "E79.1", {"start": v(80, -80) * mm, "end": v(80, 80) * mm});
            skArc(sketch, "E79.2", {"start": v(80, 80) * mm, "mid": v(77.07, 87.07) * mm, "end": v(70, 90) * mm});
            skLineSegment(sketch, "E79.3", {"start": v(-70, 90) * mm, "end": v(70, 90) * mm});
            skCircle(sketch, "E79.4", {"center": v(60, -67.5) * mm, "radius": 4 * mm});
            skArc(sketch, "E79.5", {"start": v(70, -90) * mm, "mid": v(77.07, -87.07) * mm, "end": v(80, -80) * mm});
            skLineSegment(sketch, "E79.6", {"start": v(60, 40.3) * mm, "end": v(60, -40.3) * mm});
            skLineSegment(sketch, "E79.7", {"start": v(-70, -90) * mm, "end": v(70, -90) * mm});
            skArc(sketch, "E79.8", {"start": v(-56.15, -48.18) * mm, "mid": v(0, -67.5) * mm, "end": v(56.15, -48.18) * mm});
            skArc(sketch, "E79.9", {"start": v(56.15, -48.18) * mm, "mid": v(58.99, -44.68) * mm, "end": v(60, -40.3) * mm});
            skCircle(sketch, "E79.10", {"center": v(-60, -67.5) * mm, "radius": 4 * mm});
            skArc(sketch, "E79.11", {"start": v(-80, -80) * mm, "mid": v(-77.07, -87.07) * mm, "end": v(-70, -90) * mm});
            skArc(sketch, "E79.12", {"start": v(-60, -40.3) * mm, "mid": v(-58.99, -44.68) * mm, "end": v(-56.15, -48.18) * mm});
            skLineSegment(sketch, "E79.13", {"start": v(-60, 40.3) * mm, "end": v(-60, -40.3) * mm});
            skLineSegment(sketch, "E79.14", {"start": v(-80, -80) * mm, "end": v(-80, 80) * mm});
            skArc(sketch, "E79.15", {"start": v(-70, 90) * mm, "mid": v(-77.07, 87.07) * mm, "end": v(-80, 80) * mm});
            skArc(sketch, "E79.16", {"start": v(-56.15, 48.18) * mm, "mid": v(-58.99, 44.68) * mm, "end": v(-60, 40.3) * mm});
            skArc(sketch, "E79.17", {"start": v(56.15, 48.18) * mm, "mid": v(0, 67.5) * mm, "end": v(-56.15, 48.18) * mm});
            skCircle(sketch, "E79.18", {"center": v(-60, 67.5) * mm, "radius": 4 * mm});
            skArc(sketch, "E79.19", {"start": v(60, 40.3) * mm, "mid": v(58.99, 44.68) * mm, "end": v(56.15, 48.18) * mm});
            skLineSegment(sketch, "E80", {"start": v(-33, 90) * mm, "end": v(-15, 108) * mm});
            skLineSegment(sketch, "E81", {"start": v(-15, 108) * mm, "end": v(-15, 120) * mm});
            skLineSegment(sketch, "E82", {"start": v(33, 90) * mm, "end": v(15, 108) * mm});
            skLineSegment(sketch, "E83", {"start": v(15, 108) * mm, "end": v(15, 120) * mm});
            skLineSegment(sketch, "E84", {"start": v(0, 90) * mm, "end": v(0, 120) * mm, "construction": true});
            skCircle(sketch, "E85", {"center": v(0, 120) * mm, "radius": 6 * mm});
            skArc(sketch, "E86", {"start": v(15, 120) * mm, "mid": v(0, 135) * mm, "end": v(-15, 120) * mm});
            skLineSegment(sketch, "E87", {"start": v(-80, 0) * mm, "end": v(80, 0) * mm, "construction": true});
            skArc(sketch, "E88.MirrorCS", {"start": v(-15, 120) * mm, "mid": v(0, 135) * mm, "end": v(15, 120) * mm});
            skLineSegment(sketch, "E89.MirrorCS", {"start": v(80, 0) * mm, "end": v(-80, 0) * mm, "construction": true});
            skLineSegment(sketch, "E90.MirrorCS", {"start": v(70, 90) * mm, "end": v(-70, 90) * mm});
            skCircle(sketch, "E91.MirrorC", {"center": v(0, -120) * mm, "radius": 6 * mm});
            skArc(sketch, "E92.MirrorCS", {"start": v(15, -120) * mm, "mid": v(0, -135) * mm, "end": v(-15, -120) * mm});
            skLineSegment(sketch, "E93.MirrorCS", {"start": v(15, -108) * mm, "end": v(15, -120) * mm});
            skLineSegment(sketch, "E94.MirrorCS", {"start": v(33, -90) * mm, "end": v(15, -108) * mm});
            skLineSegment(sketch, "E95.MirrorCS", {"start": v(-15, -108) * mm, "end": v(-15, -120) * mm});
            skLineSegment(sketch, "E96.MirrorCS", {"start": v(-33, -90) * mm, "end": v(-15, -108) * mm});
            skLineSegment(sketch, "E97.MirrorCS", {"start": v(0, -90) * mm, "end": v(0, -120) * mm, "construction": true});
            skCircle(sketch, "E98.0", {"center": v(-90.03, 66.09) * mm, "radius": 4 * mm});
            skLineSegment(sketch, "E98.1", {"start": v(-75.78, -58.16) * mm, "end": v(-75.78, 70.34) * mm});
            skArc(sketch, "E98.2", {"start": v(-75.78, 70.34) * mm, "mid": v(-78.7, 77.4) * mm, "end": v(-85.78, 80.34) * mm});
            skLineSegment(sketch, "E98.3", {"start": v(-214.28, 80.34) * mm, "end": v(-85.78, 80.34) * mm});
            skCircle(sketch, "E98.4", {"center": v(-90.03, -53.91) * mm, "radius": 4 * mm});
            skArc(sketch, "E98.5", {"start": v(-85.78, -68.16) * mm, "mid": v(-78.7, -65.23) * mm, "end": v(-75.78, -58.16) * mm});
            skLineSegment(sketch, "E98.6", {"start": v(-90.03, 44.92) * mm, "end": v(-90.03, -32.74) * mm});
            skLineSegment(sketch, "E98.7", {"start": v(-214.28, -68.16) * mm, "end": v(-85.78, -68.16) * mm});
            skArc(sketch, "E98.8", {"start": v(-204.28, -41.8) * mm, "mid": v(-150.03, -53.91) * mm, "end": v(-95.77, -41.8) * mm});
            skArc(sketch, "E98.9", {"start": v(-95.77, -41.8) * mm, "mid": v(-91.58, -38.1) * mm, "end": v(-90.03, -32.74) * mm});
            skCircle(sketch, "E98.10", {"center": v(-210.03, -53.91) * mm, "radius": 4 * mm});
            skArc(sketch, "E98.11", {"start": v(-224.28, -58.16) * mm, "mid": v(-221.35, -65.23) * mm, "end": v(-214.28, -68.16) * mm});
            skArc(sketch, "E98.12", {"start": v(-210.03, -32.74) * mm, "mid": v(-208.47, -38.1) * mm, "end": v(-204.28, -41.8) * mm});
            skLineSegment(sketch, "E98.13", {"start": v(-210.03, 44.92) * mm, "end": v(-210.03, -32.74) * mm});
            skLineSegment(sketch, "E98.14", {"start": v(-224.28, -58.16) * mm, "end": v(-224.28, 70.34) * mm});
            skArc(sketch, "E98.15", {"start": v(-214.28, 80.34) * mm, "mid": v(-221.35, 77.4) * mm, "end": v(-224.28, 70.34) * mm});
            skArc(sketch, "E98.16", {"start": v(-204.28, 53.97) * mm, "mid": v(-208.47, 50.28) * mm, "end": v(-210.03, 44.92) * mm});
            skArc(sketch, "E98.17", {"start": v(-95.77, 53.97) * mm, "mid": v(-150.03, 66.09) * mm, "end": v(-204.28, 53.97) * mm});
            skCircle(sketch, "E98.18", {"center": v(-210.03, 66.09) * mm, "radius": 4 * mm});
            skArc(sketch, "E98.19", {"start": v(-90.03, 44.92) * mm, "mid": v(-91.58, 50.28) * mm, "end": v(-95.77, 53.97) * mm});
            skLineSegment(sketch, "E99", {"start": v(-183.03, 80.34) * mm, "end": v(-165.03, 98.34) * mm});
            skLineSegment(sketch, "E100", {"start": v(-165.03, 98.34) * mm, "end": v(-165.03, 110.34) * mm});
            skLineSegment(sketch, "E101", {"start": v(-117.03, 80.34) * mm, "end": v(-135.03, 98.34) * mm});
            skLineSegment(sketch, "E102", {"start": v(-135.03, 98.34) * mm, "end": v(-135.03, 110.34) * mm});
            skLineSegment(sketch, "E103", {"start": v(-150.03, 80.34) * mm, "end": v(-150.03, 110.34) * mm, "construction": true});
            skCircle(sketch, "E104", {"center": v(-150.03, 110.34) * mm, "radius": 6 * mm});
            skArc(sketch, "E105", {"start": v(-135.03, 110.34) * mm, "mid": v(-150.03, 125.34) * mm, "end": v(-165.03, 110.34) * mm});
            skLineSegment(sketch, "E106", {"start": v(-224.28, 6.09) * mm, "end": v(-75.78, 6.09) * mm, "construction": true});
            skArc(sketch, "E107.MirrorCS", {"start": v(-165.03, 110.34) * mm, "mid": v(-150.03, 125.34) * mm, "end": v(-135.03, 110.34) * mm});
            skLineSegment(sketch, "E108.MirrorCS", {"start": v(-75.78, 6.09) * mm, "end": v(-224.28, 6.09) * mm, "construction": true});
            skLineSegment(sketch, "E109.MirrorCS", {"start": v(-85.78, 80.34) * mm, "end": v(-214.28, 80.34) * mm});
            skCircle(sketch, "E110.MirrorC", {"center": v(-150.03, -98.16) * mm, "radius": 6 * mm});
            skArc(sketch, "E111.MirrorCS", {"start": v(-135.03, -98.16) * mm, "mid": v(-150.03, -113.16) * mm, "end": v(-165.03, -98.16) * mm});
            skLineSegment(sketch, "E112.MirrorCS", {"start": v(-135.03, -86.16) * mm, "end": v(-135.03, -98.16) * mm});
            skLineSegment(sketch, "E113.MirrorCS", {"start": v(-117.03, -68.16) * mm, "end": v(-135.03, -86.16) * mm});
            skLineSegment(sketch, "E114.MirrorCS", {"start": v(-165.03, -86.16) * mm, "end": v(-165.03, -98.16) * mm});
            skLineSegment(sketch, "E115.MirrorCS", {"start": v(-183.03, -68.16) * mm, "end": v(-165.03, -86.16) * mm});
            skLineSegment(sketch, "E116.MirrorCS", {"start": v(-150.03, -68.16) * mm, "end": v(-150.03, -98.16) * mm, "construction": true});
            skSolve(sketch);
        }
        {
            var Q0;
            Q0=qSketchRegion(id+"F16",true);
            var Q1;
            Q1=makeQuery(id+"F2.opExtrude","CAP_FACE",FACE,{"disambiguationData":[OSD([sQuery(id+"F0.wireOp",EDGE,"E12"),sQuery(id+"F0.wireOp",EDGE,"E13"),sQuery(id+"F0.wireOp",EDGE,"E14"),sQuery(id+"F0.wireOp",EDGE,"E15"),sQuery(id+"F0.wireOp",EDGE,"E17.filletArc"),sQuery(id+"F0.wireOp",EDGE,"E18.filletArc"),sQuery(id+"F0.wireOp",EDGE,"E19.filletArc"),sQuery(id+"F0.wireOp",EDGE,"E20.filletArc"),sQuery(id+"F0.wireOp",EDGE,"E25.0"),sQuery(id+"F0.wireOp",EDGE,"E25.1"),sQuery(id+"F0.wireOp",EDGE,"E25.2"),sQuery(id+"F0.wireOp",EDGE,"E25.3"),sQuery(id+"F0.wireOp",EDGE,"E25.4"),sQuery(id+"F0.wireOp",EDGE,"E25.5"),sQuery(id+"F0.wireOp",EDGE,"E25.6"),sQuery(id+"F0.wireOp",EDGE,"E25.7")])],"isStart":false});
            extrude(context, id + "F17", {"entities" : qUnion([Q0]), "endBound" : BoundingType.UP_TO_SURFACE, "depth" : 25 * mm, "endBoundEntityFace" : qUnion([Q1]), "offsetDistance" : 25 * mm});
        }
    });
